# Revit family: РОСМА_Манометр аммиачный коррозионностойкий
name_source: partatom
category: Арматура трубопроводов
revit_build: Autodesk Revit 2018 (Build: 20180423_1000(x64)
units: mm (PartAtom-declared; Revit-internal decimal feet)

## family parameters
Всегда вертикально = Да
На основе рабочей плоскости = Нет
Общий = Нет
При загрузке вырезать с полостями = Нет
Размер круглого соединителя = Использовать диаметр
Тип детали = Вставляется

## types (2) — shared parameters
ADSK_Единица измерения = шт.
ADSK_Количество = 1
DN = 15.00 мм
Ddempfer = 6 мм
Table = спец_аммиачный коррозионностойкий
Table_2 = размеры_аммиачный коррозионностойкий
URL = https://rosma.spb.ru
Группа модели = Оборудование
Давление01 = ‎ : ТМ 0…0.6МПа(-30...+10°C)
Давление02 = ‎ : ТМ 0…1.0МПа(-30...+25°C)
Давление03 = ‎ : ТМ 0…4МПа(-30...+70°C)
Давление04 = ‎ : ТМВ -0.1…0.5МПа(-70...+5°C)
Давление05 = ‎ : ТМВ -0.1…0.9МПа(-70...+20°C)
Давление06 = ‎ : ТМВ -0.1…1.5МПа(-70...+40°C)
Давление07 = ‎ : ТМВ -0.1…2.4МПа(-70...+55°C)
Диапазон раб. температур окр. среды (без заполнения) = −60°C…+60°C
Диапазон раб. температур окр. среды (с заполнением силиконом ПМС-50) = −60°C…+60°C
Изготовитель = ЗАО "РОСМА"
Класс точности = 1
Климатическое исполнение = Группа Д2 по ГОСТ Р 52931; климатическое исполнение УХЛ категории 1.1 по ГОСТ 15150
Код IP = IP65
Межпроверочный интервал = 2 года
Описание = Тип ТМВ — NH3, серия 21. Манометры, с возможностью гидрозаполнения (виброустойчивый), предназначены для измерения избыточного и вакуумметрического давления жидкого, газообразного и водного раствора аммиака. Приборы имеют дополнительную температурную шкалу.
Техническая документация = ТУ 4212-001-4719015564-2008; ГОСТ 2405–88
лого_задн_стенка = Да

## per-type parameters (varying)
| type | Объем заполняемой жидкости, мл |
| 521 | 350 |
| 621 | 770 |

note: column(s) folded — value = type name in every type: Исполнение
